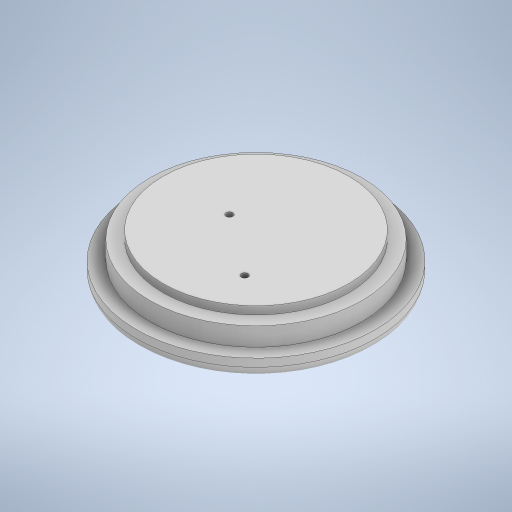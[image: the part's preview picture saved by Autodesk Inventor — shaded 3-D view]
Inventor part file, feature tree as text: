
AUTODESK INVENTOR PART (.ipt)
format: ipt  version: 2024 (Build 280153000, 153)  size: 276,480 bytes
history: native  units: mm
features: extrude x4, sketch x3, fillet x1
ambient origin geometry x8: Origin, YZ Plane, XZ Plane, XY Plane, X Axis, Y Axis, Z Axis, Center Point
bodies: Solid1 (feature_tree)
feature tree (8):
  sketch  "Sketch1"  dims[d0=80.0mm d1=70.0mm]
  extrude  "Extrusion1"  Depth=70.0mm
  extrude  "Extrusion2"  Depth=7.0mm TaperAngle=0.0deg
  extrude  "Extrusion4"  Depth=7.0mm TaperAngle=0.0deg
  fillet  "Fillet1"  Radius=4.0mm
  extrude  "Extrusion5"  Depth=5.0mm
  sketch  "Sketch3"  dims[d2=10.0mm d3=0.0mm d4=7.0mm d5=0.0mm]
  sketch  "Sketch4"  dims[d14=90.0mm d15=7.0mm d16=0.0mm d17=4.0mm d24=24.0mm d25=54.0mm d26=10.0mm d27=2.5mm d28=2.5mm d29=5.0mm d30=0.0mm]
